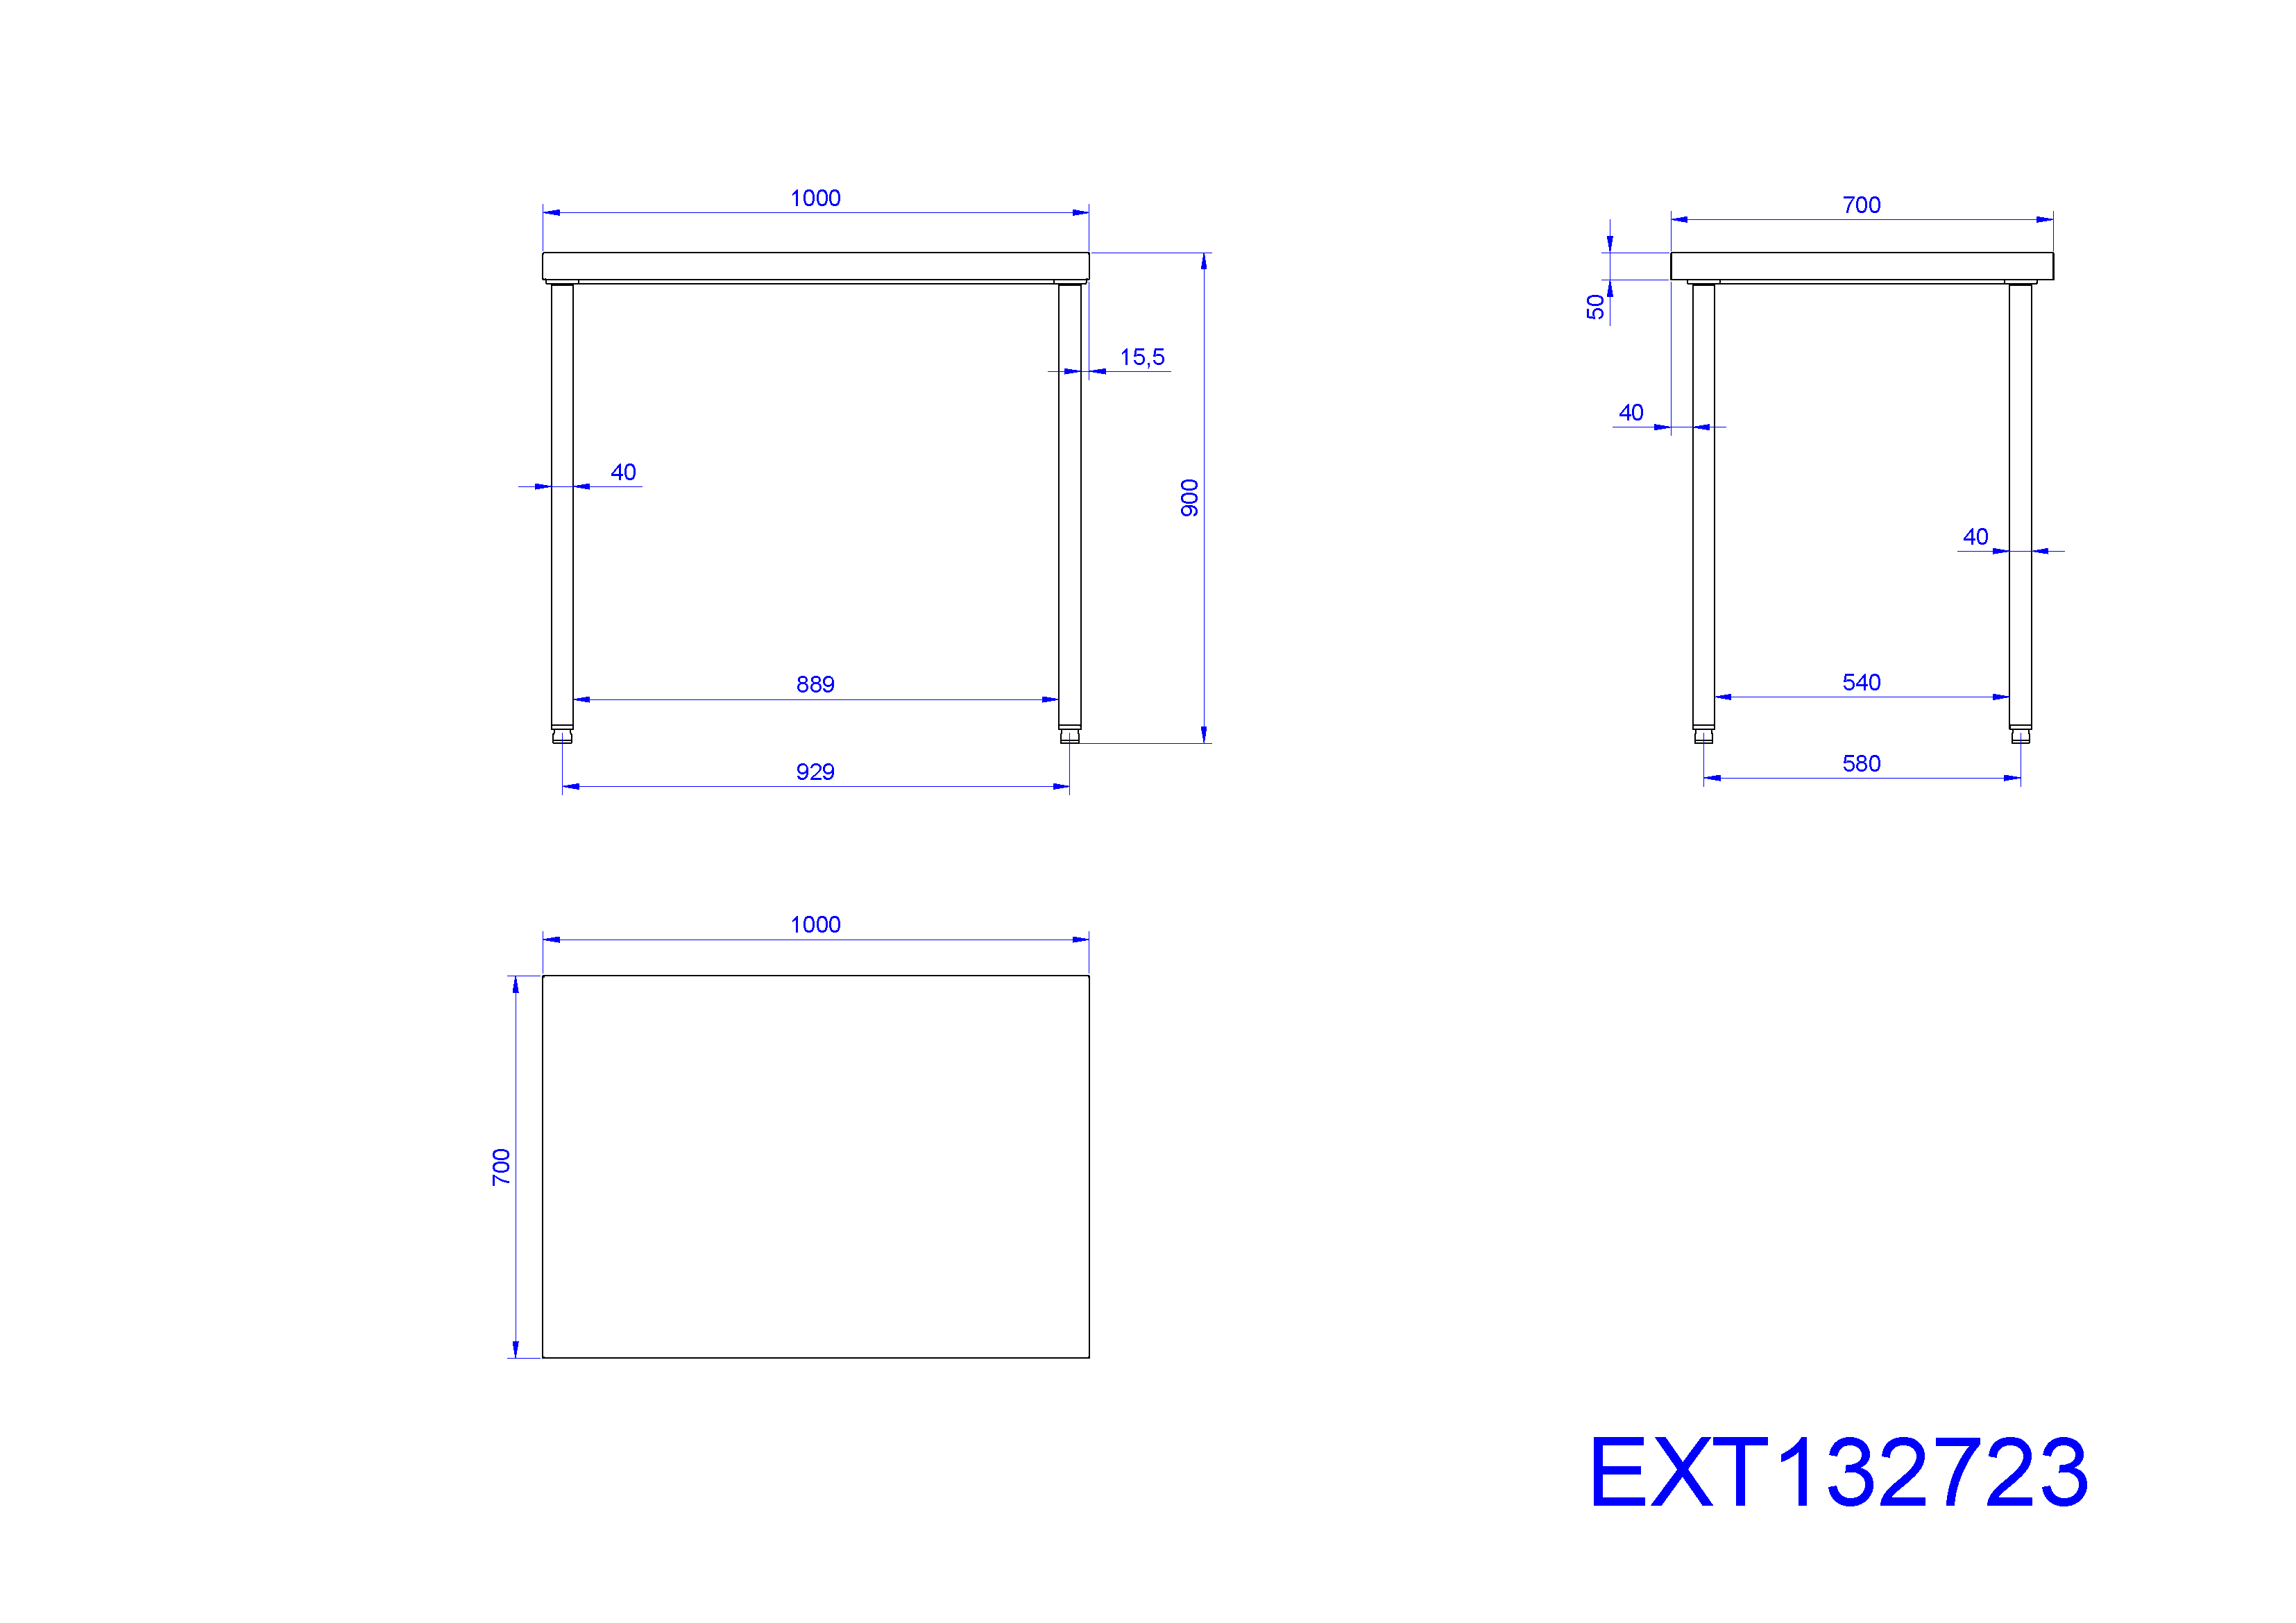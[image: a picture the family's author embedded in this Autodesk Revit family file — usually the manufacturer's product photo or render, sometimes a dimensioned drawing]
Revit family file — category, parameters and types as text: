
# Revit family: QF_ELECTROLUXPROFESSIONAL_134134_GLG1216SXP
name_source: partatom
category: Attrezzature speciali
units: mm (PartAtom-declared; Revit-internal decimal feet)

## family parameters
Basato su piano di lavoro = No
Condiviso = No
Punto di calcolo locali = No
Quota connettore circolare = Usa diametro
Sempre verticale = Sì
Taglio con vuoti quando caricato = No
Tipo di parte = Normale

## types (1)
- Standard
    Accessory = Sì
    Cold Water Size = 0 mm
    Compressed Air Pressure = 0.0 Pa
    Compressed Air Size = 0 mm
    Compressed Air Volume = 0.0 L/s
    Condensate Return Size = 0 mm
    Cycle = 0 Hz
    Depth Actual = 700 mm  [stored 2.29659 ft]
    Descrizione = SINK CUPBOARD 1 BOWL+ L/H DRAINER 1200MM
    Direct Waste Size = 0 mm
    Gas Input Pressure = 0
    Gas KW = 0
    Gas Size = 0 mm
    HP = 0 HP
    Height Actual = 1000 mm  [stored 3.28084 ft]
    Hot Water Size = 0 mm
    Item Number = 134134
    Length Actual = 1200 mm  [stored 3.93701 ft]
    Modello = GLG1216SXP
    Phase = 0
    Produttore = Electrolux Professional
    Prospetto di default = 0 mm  [stored 0 ft]
    Refrigerant Compressor Remote = Sì
    Refrigeration Liquid Line Size = 0 mm  [stored 0 ft]
    Refrigeration Suction Line Size = 0 mm  [stored 0 ft]
    Steam Consumption per Hour = 0
    Steam Supply Maximum Pressure = 0.0 Pa
    Steam Supply Minimum Pressure = 0.0 Pa
    Steam Supply Size = 0 mm
    URL = https://www.electroluxprofessional.com
    URL Manufacturer = https://www.electroluxprofessional.com
    Volts = 0 V
    Watts = 0 W
    Weight = 47.00 kg

note: source unit labels omitted for Gas Input Pressure — the stored unit's dimension contradicts the parameter name (converter mislabeling)

note: [stored X ft] marks values corroborated as IEEE doubles in the binary element streams (Revit-internal decimal feet)

## geometry (parser evidence)
native form markers: Blend x4, Sweep x4
no freeform markers — native parametric forms only
